# Revit family: 07 GFH 55 INOX
name_source: partatom
category: Air Terminals
revit_build: Autodesk Revit 2017 (Build: 20160225_1515(x64)
units: mm (PartAtom-declared; Revit-internal decimal feet)

## family parameters
Always vertical = Yes
Cut with Voids When Loaded = No
Part Type = Normal
Room Calculation Point = No
Round Connector Dimension = Use Diameter
Shared = No
Work Plane-Based = No

## types (1)
- GFH 55 INOX
    Acabado = Teka_Acero inoxidable austenítico
    Ancho = 550 mm
    Anillos_Luces = Teka_Luminarias
    Bandejas = Teka_Bandejas
    Ca_1_Frecuencia 50/60 Hz = Yes
    Ca_1_Opción de recirculación = Yes
    Ca_1_Potencia Iluminación, W. (Led) = 2x20W
    Ca_1_Potencia motor, W. = 175
    Ca_1_Potencia máxima, W. = 215
    Ca_1_Reducción opcional Ø 150/ Ø120 mm. = No
    Ca_1_Salida exterior, mm. = 132
    Ca_1_Tensión 220/240 V. = Sí
    Ca_2_Electrónico = No
    Ca_2_Pulsante (Retroiluminación) = Yes
    Ca_2_Touch Control = No
    Ca_3_Filtro metálico decorativo = No
    Ca_3_Indicador de saturación de filtros = No
    Ca_3_Motor Blindado = No
    Ca_3_N° de Velocidades = 3
    Ca_3_N° de motores = 1 DT
    Ca_3_Panel de fácil limpieza = No
    Ca_3_Piloto de funcionamiento = Yes
    Ca_3_Programación de tiempo de aspiración = No
    Ca_3_Sensor de humedad = No
    Ca_4_Ala de Cristal = No
    Ca_4_Ala de acero Inoxidable = No
    Ca_4_Fabricada en Acero Austenítico Certificado = Yes
    Ca_Alto = 175 mm  [stored 0.574147 ft]
    Ca_Ancho = 550 mm
    Ca_Creado por = Catálogo Arquitectura
    Ca_Código Catálogo Arquitectura = 465_TEK_042
    Ca_Código EAN = 8421152036396
    Ca_Código del Producto = 40446700
    Ca_Especificaciones Técnicas = Campana integrable a mueble de cocina modelo GFH 55
    Ca_Fabricante = Teka
    Ca_Instalación = Empotrable
    Ca_Itemizado CDT = E 08 06 02
    Ca_Masterformat = 11 30 13.13
    Ca_Material Principal = Acero Austenítico Certificado
    Ca_Medidas de embalaje = 60 x 47 x 36
    Ca_País de Fabricación = Portugal
    Ca_Peso = 7,0 kg
    Ca_Producto = Campana tipo grupo filtrante GFH 55
    Ca_Profundidad = 310 mm  [stored 1.01706 ft]
    Ca_Representante = Teka
    Ca_Teléfono = 99821 1017
    Ca_Usos = Campana de extracción y recirculación de cocina
    Ca_Web del Fabricante = www.teka.com
    Ca_Web del Representante = www.teka.cl
    Description = Campana de extracción y recirculación de cocina (NO incluye filtros de Carbón)
    Interior Mate = Teka_Interior Mate
    Manufacturer = Teka
    Model = GFH 55
    Profundidad = 289 mm
    URL = www.teka.cl

note: [stored X ft] marks values corroborated as IEEE doubles in the binary element streams (Revit-internal decimal feet)

## geometry (parser evidence)
native form markers: Sweep x3
no freeform markers — native parametric forms only
